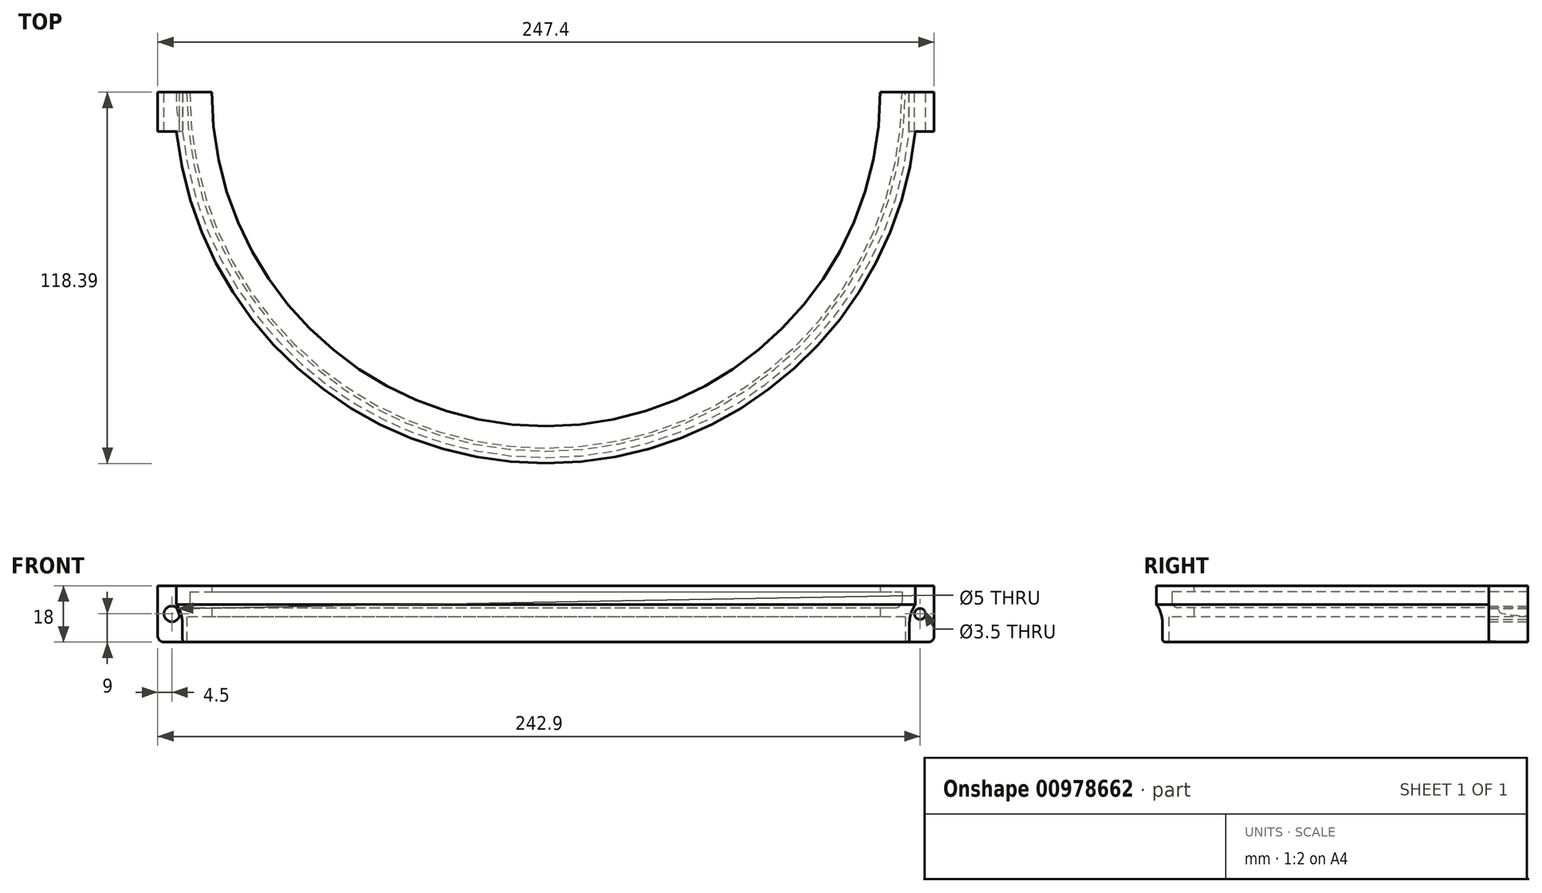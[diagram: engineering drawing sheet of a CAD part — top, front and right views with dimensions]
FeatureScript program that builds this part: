
annotation { "Feature Type Name" : "Feature", "Feature Type Description" : "" }
export const myFeature = defineFeature(function(context is Context, id is Id, definition is map)
    precondition{}
    {
        {
            var Q0;
            Q0=qCreatedBy(makeId("Front.planeOp"),FACE);
            var sketch = newSketch(context, id + "F0", { "sketchPlane" : qUnion([Q0])});
            skLineSegment(sketch, "E0", {"start": v(0, 0) * mm, "end": v(-112.5, 0) * mm});
            skLineSegment(sketch, "E1", {"start": v(-106.5, -3) * mm, "end": v(-114.5, -3) * mm});
            skLineSegment(sketch, "E2", {"start": v(-114.5, -3) * mm, "end": v(-114.5, -11) * mm});
            skLineSegment(sketch, "E3", {"start": v(-114.5, -11) * mm, "end": v(-116.5, -11) * mm});
            skLineSegment(sketch, "E4", {"start": v(-106.89, 7) * mm, "end": v(-118.39, 7) * mm});
            skLineSegment(sketch, "E5", {"start": v(-116.5, -11) * mm, "end": v(-116.5, -5) * mm});
            skLineSegment(sketch, "E6", {"start": v(-118.39, 7) * mm, "end": v(-118.39, 1) * mm});
            skLineSegment(sketch, "E7", {"start": v(0, -15.27) * mm, "end": v(0, 14.73) * mm});
            skLineSegment(sketch, "E8", {"start": v(-106.5, -3) * mm, "end": v(-106.5, 7) * mm});
            skLineSegment(sketch, "E9", {"start": v(-106.89, 7) * mm, "end": v(-106.5, 7) * mm});
            skArc(sketch, "E10", {"start": v(-116.5, -5) * mm, "mid": v(-116.98, -1.85) * mm, "end": v(-118.39, 1) * mm});
            skSolve(sketch);
        }
        {
            var Q0;
            Q0=qSketchRegion(id+"F0",true);
            var Q1;
            Q1=sQuery(id+"F0.wireOp",EDGE,"E7");
            revolve(context, id + "F1", {"surfaceOperationType" : NewSurfaceOperationType.NEW, "entities" : qUnion([Q0]), "axis" : qUnion([Q1]), "revolveType" : RevolveType.FULL});
        }
        {
            var Q0;
            Q0=qCreatedBy(makeId("Top.planeOp"),FACE);
            var sketch = newSketch(context, id + "F2", { "sketchPlane" : qUnion([Q0])});
            skCircle(sketch, "E11", {"center": v(0, 0) * mm, "radius": 113.5 * mm});
            skSolve(sketch);
        }
        {
            var Q0;
            Q0=qSketchRegion(id+"F2",true);
            extrude(context, id + "F3", {"entities" : qUnion([Q0]), "operationType" : NewBodyOperationType.REMOVE, "depth" : 5 * mm, "offsetDistance" : 25 * mm});
        }
        {
            var Q0;
            Q0=makeQuery(id+"F1.opRevolve","SWEPT_EDGE",EDGE,{"disambiguationData":[OSD([sQuery(id+"F0.wireOp",EDGE,"E3"),sQuery(id+"F0.wireOp",EDGE,"E5")])]});
            fillet(context, id + "F4", {"entities" : qUnion([Q0]), "radius" : 1 * mm, "tangentPropagation" : true, "allowEdgeOverflow" : false});
        }
        {
            var Q0;
            Q0=qCreatedBy(makeId("Front.planeOp"),FACE);
            var sketch = newSketch(context, id + "F5", { "sketchPlane" : qUnion([Q0])});
            skLineSegment(sketch, "E12.bottom", {"start": v(-115.7, 7) * mm, "end": v(-123.7, 7) * mm});
            skLineSegment(sketch, "E12.top", {"start": v(-115.7, -11) * mm, "end": v(-123.7, -11) * mm});
            skLineSegment(sketch, "E12.left", {"start": v(-115.7, 7) * mm, "end": v(-115.7, -11) * mm});
            skLineSegment(sketch, "E12.right", {"start": v(-123.7, 7) * mm, "end": v(-123.7, -11) * mm});
            skCircle(sketch, "E13", {"center": v(-119.2, -2) * mm, "radius": 2.5 * mm});
            skSolve(sketch);
        }
        {
            var Q0;
            Q0=qCreatedBy(makeId("Front.planeOp"),FACE);
            var sketch = newSketch(context, id + "F6", { "sketchPlane" : qUnion([Q0])});
            skLineSegment(sketch, "E14.bottom", {"start": v(123.7, 7) * mm, "end": v(115.7, 7) * mm});
            skLineSegment(sketch, "E14.top", {"start": v(123.7, -11) * mm, "end": v(115.7, -11) * mm});
            skLineSegment(sketch, "E14.left", {"start": v(123.7, 7) * mm, "end": v(123.7, -11) * mm});
            skLineSegment(sketch, "E14.right", {"start": v(115.7, 7) * mm, "end": v(115.7, -11) * mm});
            skCircle(sketch, "E15", {"center": v(119.2, -2) * mm, "radius": 1.75 * mm});
            skSolve(sketch);
        }
        {
            var Q0;
            Q0=qSketchRegion(id+"F5",true);
            extrude(context, id + "F7", {"entities" : qUnion([Q0]), "operationType" : NewBodyOperationType.ADD, "endBound" : BoundingType.SYMMETRIC, "depth" : 25 * mm, "offsetDistance" : 25 * mm});
        }
        {
            var Q0;
            Q0=qSketchRegion(id+"F6",true);
            extrude(context, id + "F8", {"entities" : qUnion([Q0]), "operationType" : NewBodyOperationType.ADD, "endBound" : BoundingType.SYMMETRIC, "depth" : 25 * mm, "offsetDistance" : 25 * mm});
        }
        {
            var Q0;
            Q0=qCreatedBy(makeId("Front.planeOp"),FACE);
            var sketch = newSketch(context, id + "F9", { "sketchPlane" : qUnion([Q0])});
            skLineSegment(sketch, "E16.bottom", {"start": v(-124.88, 17.7) * mm, "end": v(125.12, 17.7) * mm});
            skLineSegment(sketch, "E16.top", {"start": v(-124.88, -82.3) * mm, "end": v(125.12, -82.3) * mm});
            skLineSegment(sketch, "E16.left", {"start": v(-124.88, 17.7) * mm, "end": v(-124.88, -82.3) * mm});
            skLineSegment(sketch, "E16.right", {"start": v(125.12, 17.7) * mm, "end": v(125.12, -82.3) * mm});
            skSolve(sketch);
        }
        {
            var Q0;
            Q0=qSketchRegion(id+"F9",true);
            extrude(context, id + "F10", {"entities" : qUnion([Q0]), "operationType" : NewBodyOperationType.REMOVE, "oppositeDirection" : true, "depth" : 150 * mm, "offsetDistance" : 25 * mm});
        }
        {
            var Q0;
            Q0=makeQuery(id+"F3.boolean.opBoolean","COPY",EDGE,{"derivedFrom":makeQuery(id+"F3.opExtrude","CAP_EDGE",EDGE,{"disambiguationData":[OSD([sQuery(id+"F2.wireOp",EDGE,"E11")])],"isStart":true})});
            fillet(context, id + "F11", {"entities" : qUnion([Q0]), "radius" : 2 * mm, "tangentPropagation" : true, "allowEdgeOverflow" : false});
        }
        {
            var Q0;
            Q0=makeQuery(id+"F8.opExtrude","SWEPT_EDGE",EDGE,{"disambiguationData":[OSD([sQuery(id+"F6.wireOp",EDGE,"E14.top"),sQuery(id+"F6.wireOp",EDGE,"E14.left")])]});
            var Q1;
            Q1=makeQuery(id+"F7.opExtrude","SWEPT_EDGE",EDGE,{"disambiguationData":[OSD([sQuery(id+"F5.wireOp",EDGE,"E12.top"),sQuery(id+"F5.wireOp",EDGE,"E12.right")])]});
            fillet(context, id + "F12", {"entities" : qUnion([Q0, Q1]), "radius" : 2 * mm, "tangentPropagation" : true, "allowEdgeOverflow" : false});
        }
    });
